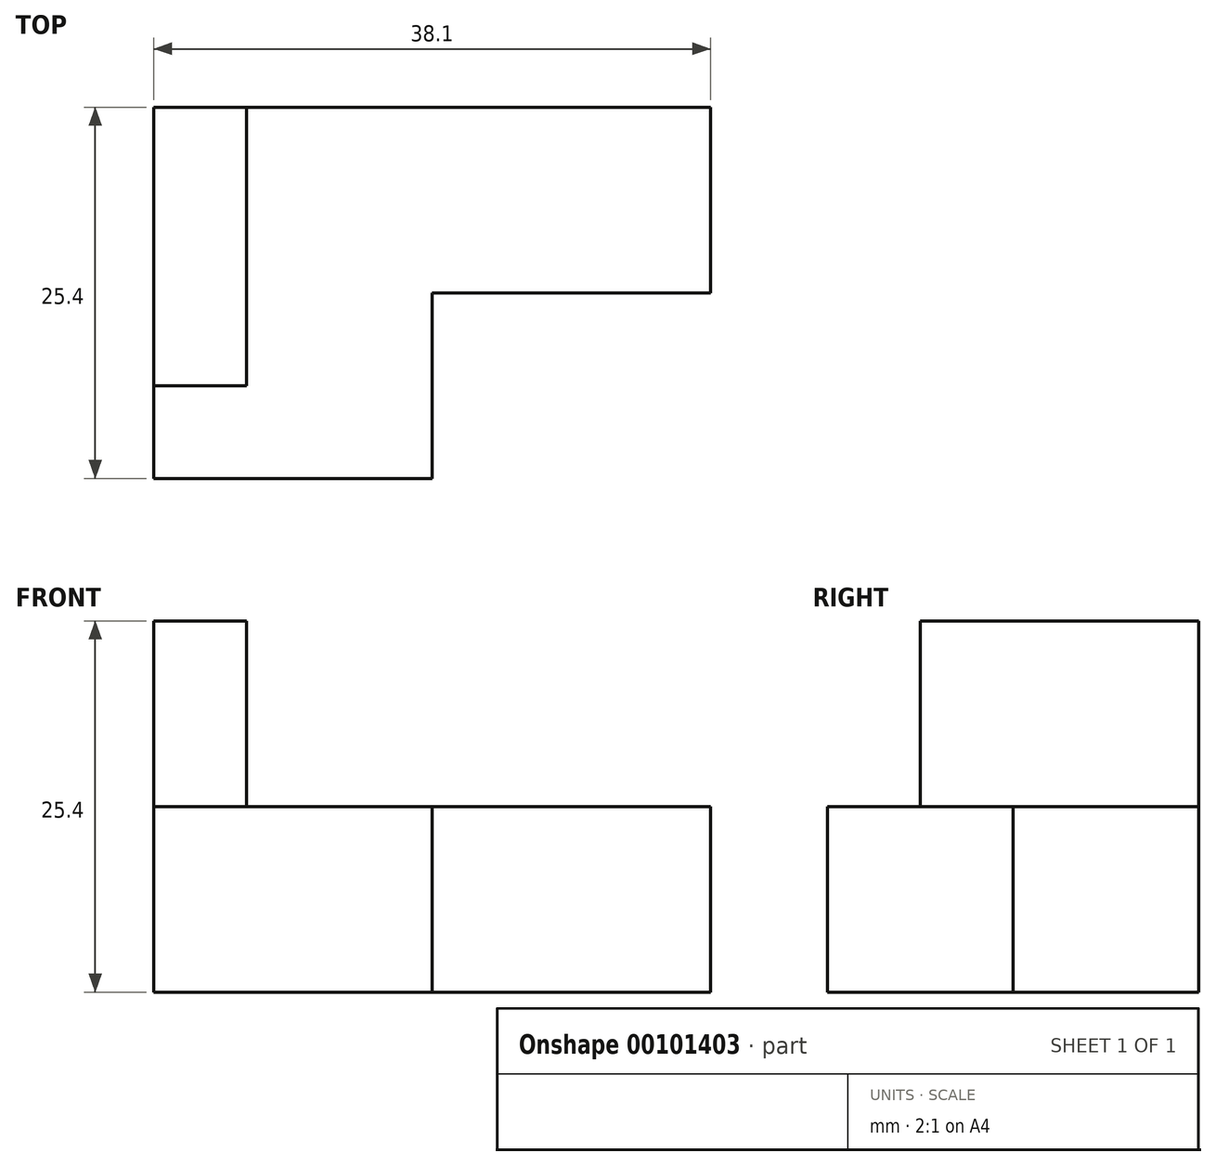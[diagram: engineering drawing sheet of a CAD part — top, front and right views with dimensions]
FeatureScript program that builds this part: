
annotation { "Feature Type Name" : "Feature", "Feature Type Description" : "" }
export const myFeature = defineFeature(function(context is Context, id is Id, definition is map)
    precondition{}
    {
        {
            var Q0;
            Q0=qCreatedBy(makeId("Front.planeOp"),FACE);
            var sketch = newSketch(context, id + "F0", { "sketchPlane" : qUnion([Q0])});
            skLineSegment(sketch, "E0", {"start": v(0, 0) * mm, "end": v(19.05, 0) * mm});
            skLineSegment(sketch, "E1", {"start": v(19.05, 0) * mm, "end": v(19.05, 12.7) * mm});
            skLineSegment(sketch, "E2", {"start": v(19.05, 12.7) * mm, "end": v(0, 12.7) * mm});
            skLineSegment(sketch, "E3", {"start": v(0, 12.7) * mm, "end": v(0, 0) * mm});
            skLineSegment(sketch, "E4", {"start": v(0, 12.7) * mm, "end": v(0, 25.4) * mm});
            skLineSegment(sketch, "E5", {"start": v(0, 25.4) * mm, "end": v(6.35, 25.4) * mm});
            skLineSegment(sketch, "E6", {"start": v(6.35, 25.4) * mm, "end": v(6.35, 12.7) * mm});
            skLineSegment(sketch, "E7", {"start": v(6.35, 12.7) * mm, "end": v(38.1, 12.7) * mm});
            skPoint(sketch, "E7.endSnap0", {"position": v(9.53, 12.7) * mm});
            skLineSegment(sketch, "E8", {"start": v(38.1, 12.7) * mm, "end": v(38.1, 0) * mm});
            skLineSegment(sketch, "E9", {"start": v(38.1, 0) * mm, "end": v(19.05, 0) * mm});
            skSolve(sketch);
        }
        {
            var Q0;
            Q0=makeQuery(id+"F0.imprint","IMPRINT",FACE,{"disambiguationData":[TD([[makeQuery(id+"F0.imprint","IMPRINT",EDGE,{"derivedFrom":sQuery(id+"F0.wireOp",EDGE,"E0")}),1.0]])]});
            extrude(context, id + "F1", {"entities" : qUnion([Q0]), "depth" : 25.4 * mm});
        }
        {
            var Q0;
            Q0=makeQuery(id+"F0.imprint","IMPRINT",FACE,{"disambiguationData":[TD([[makeQuery(id+"F0.imprint","IMPRINT",EDGE,{"derivedFrom":sQuery(id+"F0.wireOp",EDGE,"E2")}),-1.0]])]});
            extrude(context, id + "F2", {"entities" : qUnion([Q0]), "operationType" : NewBodyOperationType.ADD, "depth" : 19.05 * mm});
        }
        {
            var Q0;
            {var subQ0=sQuery(id+"F0.wireOp",EDGE,"E1");Q0=makeQuery(id+"F0.imprint","IMPRINT",FACE,{"disambiguationData":[TD([[makeQuery(id+"F0.imprint","IMPRINT",EDGE,{"derivedFrom":subQ0}),-1.0]])]});}
            extrude(context, id + "F3", {"entities" : qUnion([Q0]), "operationType" : NewBodyOperationType.ADD, "depth" : 12.7 * mm});
        }
    });
